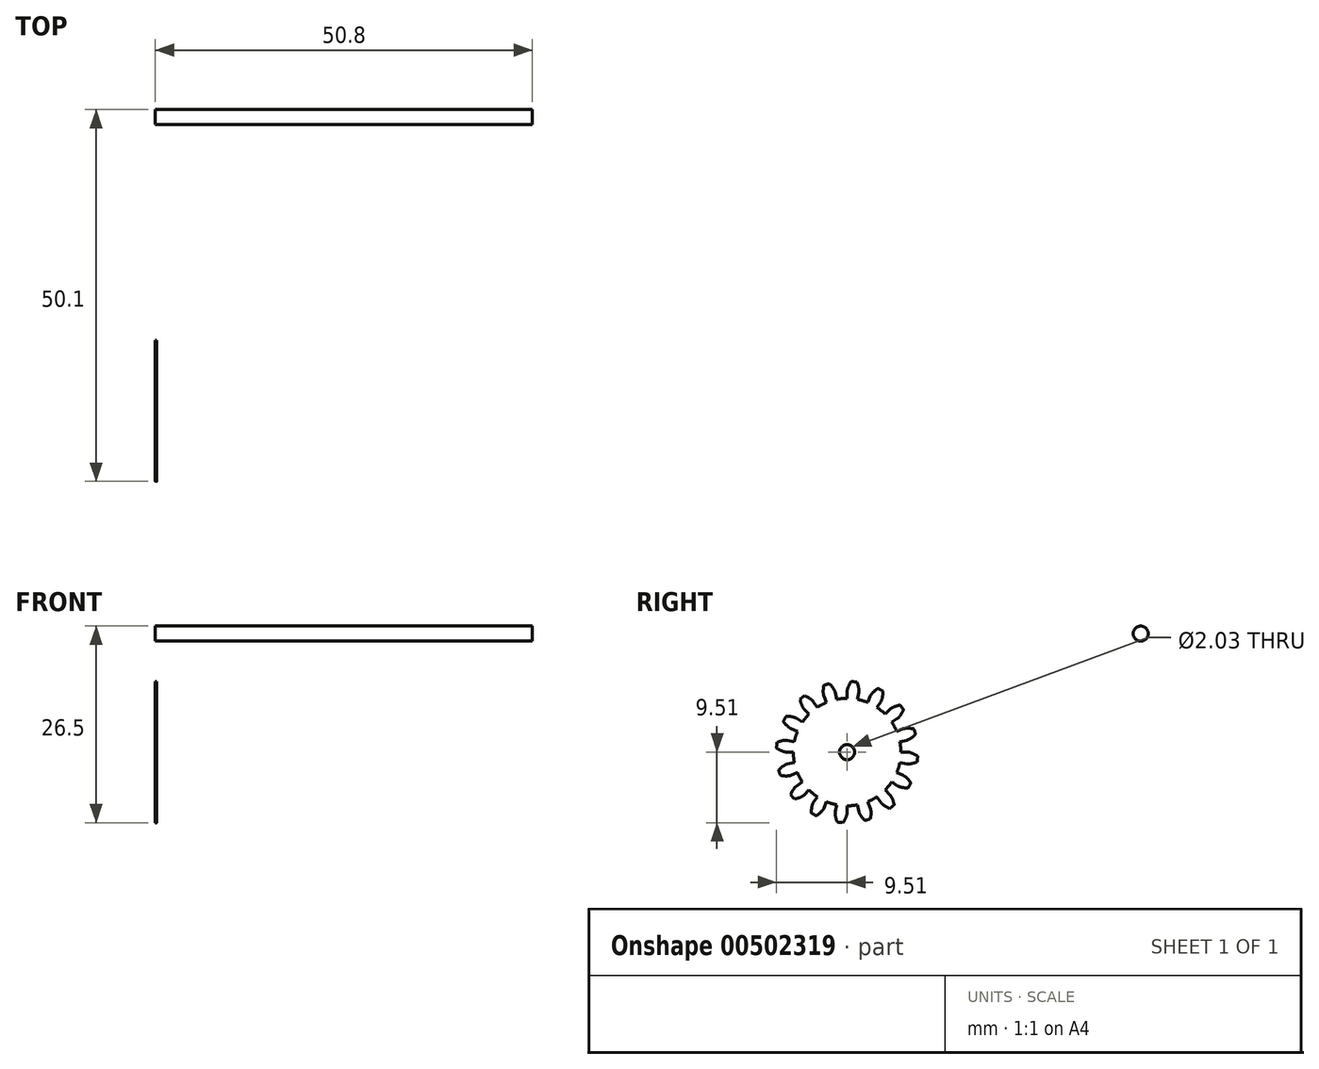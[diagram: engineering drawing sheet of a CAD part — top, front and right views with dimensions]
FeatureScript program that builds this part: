
annotation { "Feature Type Name" : "Feature", "Feature Type Description" : "" }
export const myFeature = defineFeature(function(context is Context, id is Id, definition is map)
    precondition{}
    {
        {
            assignVariable(context, id + "F0", {"name" : "NumberTeeth", "anyValue" : 16});
        }
        {
            assignVariable(context, id + "F1", {"name" : "GearThickness", "anyValue" : .16});
        }
        {
            var Q0;
            Q0=qCreatedBy(makeId("Right.planeOp"),FACE);
            var sketch = newSketch(context, id + "F2", { "sketchPlane" : qUnion([Q0])});
            skCircle(sketch, "E0", {"center": v(0, 0) * mm, "radius": 7.24 * mm});
            skCircle(sketch, "E1", {"center": v(0, 0) * mm, "radius": 8.2 * mm, "construction": true});
            skCircle(sketch, "E2", {"center": v(0, 0) * mm, "radius": 8.47 * mm, "construction": true});
            skCircle(sketch, "E3", {"center": v(0, 0) * mm, "radius": 9.53 * mm});
            skLineSegment(sketch, "E4", {"start": v(0, 0) * mm, "end": v(-8.2, 0) * mm, "construction": true});
            skLineSegment(sketch, "E5.1.0", {"start": v(0, 0) * mm, "end": v(-8.19, 0.4) * mm, "construction": true});
            skLineSegment(sketch, "E5.2.0", {"start": v(0, 0) * mm, "end": v(-8.16, 0.82) * mm, "construction": true});
            skLineSegment(sketch, "E5.3.0", {"start": v(0, 0) * mm, "end": v(-8.1, 1.22) * mm, "construction": true});
            skLineSegment(sketch, "E5.4.0", {"start": v(0, 0) * mm, "end": v(-8.03, 1.63) * mm, "construction": true});
            skLineSegment(sketch, "E5.5.0", {"start": v(0, 0) * mm, "end": v(-7.94, 2.03) * mm, "construction": true});
            skLineSegment(sketch, "E5.6.0", {"start": v(0, 0) * mm, "end": v(-7.83, 2.42) * mm, "construction": true});
            skLineSegment(sketch, "E5.7.0", {"start": v(0, 0) * mm, "end": v(-7.7, 2.81) * mm, "construction": true});
            skLineSegment(sketch, "E5.8.0", {"start": v(0, 0) * mm, "end": v(-7.55, 3.2) * mm, "construction": true});
            skLineSegment(sketch, "E5.9.0", {"start": v(0, 0) * mm, "end": v(-7.38, 3.57) * mm, "construction": true});
            skLineSegment(sketch, "E5.10.0", {"start": v(0, 0) * mm, "end": v(-7.2, 3.93) * mm, "construction": true});
            skLineSegment(sketch, "E5.11.0", {"start": v(0, 0) * mm, "end": v(-6.99, 4.28) * mm, "construction": true});
            skLineSegment(sketch, "E5.12.0", {"start": v(0, 0) * mm, "end": v(-6.77, 4.63) * mm, "construction": true});
            skLineSegment(sketch, "E5.13.0", {"start": v(0, 0) * mm, "end": v(-6.53, 4.96) * mm, "construction": true});
            skLineSegment(sketch, "E5.14.0", {"start": v(0, 0) * mm, "end": v(-6.27, 5.28) * mm, "construction": true});
            skLineSegment(sketch, "E5.anchor2", {"start": v(0, 0) * mm, "end": v(-6.27, 5.28) * mm, "construction": true});
            skLineSegment(sketch, "E6", {"start": v(-8.19, 0.4) * mm, "end": v(-8.2, 0) * mm, "construction": true});
            skLineSegment(sketch, "E7", {"start": v(-8.16, 0.82) * mm, "end": v(-8.24, 0) * mm, "construction": true});
            skLineSegment(sketch, "E8", {"start": v(-8.1, 1.22) * mm, "end": v(-8.29, 0) * mm, "construction": true});
            skLineSegment(sketch, "E9", {"start": v(-7.94, 2.03) * mm, "end": v(-8.45, 0.04) * mm, "construction": true});
            skLineSegment(sketch, "E10", {"start": v(-7.83, 2.42) * mm, "end": v(-8.56, 0.07) * mm, "construction": true});
            skLineSegment(sketch, "E11", {"start": v(-7.7, 2.81) * mm, "end": v(-8.68, 0.12) * mm, "construction": true});
            skLineSegment(sketch, "E12", {"start": v(-7.55, 3.2) * mm, "end": v(-8.83, 0.17) * mm, "construction": true});
            skLineSegment(sketch, "E13", {"start": v(-7.38, 3.57) * mm, "end": v(-8.99, 0.24) * mm, "construction": true});
            skLineSegment(sketch, "E14", {"start": v(-7.2, 3.93) * mm, "end": v(-9.16, 0.33) * mm, "construction": true});
            skLineSegment(sketch, "E15", {"start": v(-6.99, 4.28) * mm, "end": v(-9.34, 0.44) * mm, "construction": true});
            skLineSegment(sketch, "E16", {"start": v(-8.03, 1.63) * mm, "end": v(-8.36, 0.02) * mm, "construction": true});
            skLineSegment(sketch, "E17", {"start": v(-6.77, 4.63) * mm, "end": v(-9.54, 0.57) * mm, "construction": true});
            skLineSegment(sketch, "E18", {"start": v(-6.53, 4.96) * mm, "end": v(-9.75, 0.72) * mm, "construction": true});
            skLineSegment(sketch, "E19", {"start": v(-6.27, 5.28) * mm, "end": v(-9.97, 0.9) * mm, "construction": true});
            skLineSegment(sketch, "E20", {"start": v(0, 0) * mm, "end": v(-8.16, 0.8) * mm, "construction": true});
            skLineSegment(sketch, "E21", {"start": v(-7.24, 0) * mm, "end": v(-8.2, 0) * mm});
            skLineSegment(sketch, "E22.MirrorCS", {"start": v(-7.1, 1.41) * mm, "end": v(-8.04, 1.6) * mm});
            skFitSpline(sketch, "E23", {"points": [v(-8.2, 0) * mm, v(-8.2, 0) * mm, v(-8.24, 0) * mm, v(-8.29, 0) * mm, v(-8.36, 0.02) * mm, v(-8.45, 0.04) * mm, v(-8.56, 0.07) * mm, v(-8.68, 0.12) * mm, v(-8.83, 0.17) * mm, v(-8.99, 0.24) * mm, v(-9.16, 0.33) * mm, v(-9.34, 0.44) * mm, v(-9.54, 0.57) * mm, v(-9.75, 0.72) * mm, v(-9.97, 0.9) * mm], "startDerivative": vector(-0.86, 0) * mm, "endDerivative": vector(-1, 0.85) * mm});
            skLineSegment(sketch, "E24", {"start": v(-9.97, 0.9) * mm, "end": v(-15.8, 5.8) * mm, "construction": true});
            skFitSpline(sketch, "E25.MirrorCS", {"points": [v(-8.04, 1.6) * mm, v(-8.05, 1.6) * mm, v(-8.08, 1.6) * mm, v(-8.13, 1.6) * mm, v(-8.2, 1.6) * mm, v(-8.3, 1.6) * mm, v(-8.4, 1.6) * mm, v(-8.54, 1.58) * mm, v(-8.7, 1.55) * mm, v(-8.86, 1.51) * mm, v(-9.05, 1.46) * mm, v(-9.25, 1.4) * mm, v(-9.47, 1.3) * mm, v(-9.7, 1.2) * mm, v(-9.95, 1.07) * mm], "startDerivative": vector(-0.85, 0.17) * mm, "endDerivative": vector(-1.15, -0.63) * mm});
            skCircle(sketch, "E26", {"center": v(0, 0) * mm, "radius": 1.02 * mm});
            skCircle(sketch, "E27", {"center": v(39.57, 15.97) * mm, "radius": 1.02 * mm});
            skSolve(sketch);
        }
        {
            var Q0;
            {var subQ0=sQuery(id+"F2.wireOp",EDGE,"E0");var subQ27=makeQuery(id+"F2.imprint","INTERSECT",VERTEX,{"derivedFrom":[subQ0,sQuery(id+"F2.wireOp",EDGE,"10ea1024-8cf5-41f5-a75f-a634b86921f3.10.0")]});Q0=makeQuery(id+"F2.imprint","IMPRINT",FACE,{"disambiguationData":[TD([[makeQuery(id+"F2.imprint","IMPRINT",EDGE,{"disambiguationData":[TD([[subQ27,-1.0]])],"derivedFrom":subQ0}),1.0]])]});}
            var Q1;
            {var subQ0=sQuery(id+"F2.wireOp",EDGE,"10ea1024-8cf5-41f5-a75f-a634b86921f3.1.0");Q1=makeQuery(id+"F2.imprint","IMPRINT",FACE,{"disambiguationData":[TD([[makeQuery(id+"F2.imprint","IMPRINT",EDGE,{"derivedFrom":subQ0}),-1.0]])]});}
            var Q2;
            {var subQ7=sQuery(id+"F2.wireOp",EDGE,"10ea1024-8cf5-41f5-a75f-a634b86921f3.2.0");Q2=makeQuery(id+"F2.imprint","IMPRINT",FACE,{"disambiguationData":[TD([[makeQuery(id+"F2.imprint","IMPRINT",EDGE,{"derivedFrom":subQ7}),-1.0]])]});}
            var Q3;
            {var subQ8=sQuery(id+"F2.wireOp",EDGE,"10ea1024-8cf5-41f5-a75f-a634b86921f3.3.0");Q3=makeQuery(id+"F2.imprint","IMPRINT",FACE,{"disambiguationData":[TD([[makeQuery(id+"F2.imprint","IMPRINT",EDGE,{"derivedFrom":subQ8}),-1.0]])]});}
            var Q4;
            {var subQ2=sQuery(id+"F2.wireOp",EDGE,"10ea1024-8cf5-41f5-a75f-a634b86921f3.4.0");Q4=makeQuery(id+"F2.imprint","IMPRINT",FACE,{"disambiguationData":[TD([[makeQuery(id+"F2.imprint","IMPRINT",EDGE,{"derivedFrom":subQ2}),-1.0]])]});}
            var Q5;
            {var subQ8=sQuery(id+"F2.wireOp",EDGE,"10ea1024-8cf5-41f5-a75f-a634b86921f3.5.0");Q5=makeQuery(id+"F2.imprint","IMPRINT",FACE,{"disambiguationData":[TD([[makeQuery(id+"F2.imprint","IMPRINT",EDGE,{"derivedFrom":subQ8}),-1.0]])]});}
            var Q6;
            {var subQ3=sQuery(id+"F2.wireOp",EDGE,"10ea1024-8cf5-41f5-a75f-a634b86921f3.6.0");Q6=makeQuery(id+"F2.imprint","IMPRINT",FACE,{"disambiguationData":[TD([[makeQuery(id+"F2.imprint","IMPRINT",EDGE,{"derivedFrom":subQ3}),-1.0]])]});}
            var Q7;
            {var subQ0=sQuery(id+"F2.wireOp",EDGE,"10ea1024-8cf5-41f5-a75f-a634b86921f3.7.0");Q7=makeQuery(id+"F2.imprint","IMPRINT",FACE,{"disambiguationData":[TD([[makeQuery(id+"F2.imprint","IMPRINT",EDGE,{"derivedFrom":subQ0}),-1.0]])]});}
            var Q8;
            {var subQ5=sQuery(id+"F2.wireOp",EDGE,"10ea1024-8cf5-41f5-a75f-a634b86921f3.8.0");Q8=makeQuery(id+"F2.imprint","IMPRINT",FACE,{"disambiguationData":[TD([[makeQuery(id+"F2.imprint","IMPRINT",EDGE,{"derivedFrom":subQ5}),-1.0]])]});}
            var Q9;
            {var subQ1=sQuery(id+"F2.wireOp",EDGE,"10ea1024-8cf5-41f5-a75f-a634b86921f3.9.0");Q9=makeQuery(id+"F2.imprint","IMPRINT",FACE,{"disambiguationData":[TD([[makeQuery(id+"F2.imprint","IMPRINT",EDGE,{"derivedFrom":subQ1}),-1.0]])]});}
            var Q10;
            {var subQ5=sQuery(id+"F2.wireOp",EDGE,"10ea1024-8cf5-41f5-a75f-a634b86921f3.10.0");Q10=makeQuery(id+"F2.imprint","IMPRINT",FACE,{"disambiguationData":[TD([[makeQuery(id+"F2.imprint","IMPRINT",EDGE,{"derivedFrom":subQ5}),-1.0]])]});}
            var Q11;
            {var subQ8=sQuery(id+"F2.wireOp",EDGE,"10ea1024-8cf5-41f5-a75f-a634b86921f3.11.0");Q11=makeQuery(id+"F2.imprint","IMPRINT",FACE,{"disambiguationData":[TD([[makeQuery(id+"F2.imprint","IMPRINT",EDGE,{"derivedFrom":subQ8}),-1.0]])]});}
            var Q12;
            {var subQ2=sQuery(id+"F2.wireOp",EDGE,"10ea1024-8cf5-41f5-a75f-a634b86921f3.12.0");Q12=makeQuery(id+"F2.imprint","IMPRINT",FACE,{"disambiguationData":[TD([[makeQuery(id+"F2.imprint","IMPRINT",EDGE,{"derivedFrom":subQ2}),-1.0]])]});}
            var Q13;
            {var subQ3=sQuery(id+"F2.wireOp",EDGE,"10ea1024-8cf5-41f5-a75f-a634b86921f3.13.0");Q13=makeQuery(id+"F2.imprint","IMPRINT",FACE,{"disambiguationData":[TD([[makeQuery(id+"F2.imprint","IMPRINT",EDGE,{"derivedFrom":subQ3}),-1.0]])]});}
            var Q14;
            {var subQ0=sQuery(id+"F2.wireOp",EDGE,"10ea1024-8cf5-41f5-a75f-a634b86921f3.14.0");Q14=makeQuery(id+"F2.imprint","IMPRINT",FACE,{"disambiguationData":[TD([[makeQuery(id+"F2.imprint","IMPRINT",EDGE,{"derivedFrom":subQ0}),-1.0]])]});}
            var Q15;
            {var subQ6=sQuery(id+"F2.wireOp",EDGE,"10ea1024-8cf5-41f5-a75f-a634b86921f3.15.0");Q15=makeQuery(id+"F2.imprint","IMPRINT",FACE,{"disambiguationData":[TD([[makeQuery(id+"F2.imprint","IMPRINT",EDGE,{"derivedFrom":subQ6}),-1.0]])]});}
            var Q16;
            {var subQ5=sQuery(id+"F2.wireOp",EDGE,"10ea1024-8cf5-41f5-a75f-a634b86921f3.16.0");Q16=makeQuery(id+"F2.imprint","IMPRINT",FACE,{"disambiguationData":[TD([[makeQuery(id+"F2.imprint","IMPRINT",EDGE,{"derivedFrom":subQ5}),-1.0]])]});}
            var Q17;
            {var subQ7=sQuery(id+"F2.wireOp",EDGE,"10ea1024-8cf5-41f5-a75f-a634b86921f3.17.0");Q17=makeQuery(id+"F2.imprint","IMPRINT",FACE,{"disambiguationData":[TD([[makeQuery(id+"F2.imprint","IMPRINT",EDGE,{"derivedFrom":subQ7}),-1.0]])]});}
            var Q18;
            {var subQ5=sQuery(id+"F2.wireOp",EDGE,"10ea1024-8cf5-41f5-a75f-a634b86921f3.18.0");Q18=makeQuery(id+"F2.imprint","IMPRINT",FACE,{"disambiguationData":[TD([[makeQuery(id+"F2.imprint","IMPRINT",EDGE,{"derivedFrom":subQ5}),-1.0]])]});}
            var Q19;
            {var subQ8=sQuery(id+"F2.wireOp",EDGE,"10ea1024-8cf5-41f5-a75f-a634b86921f3.19.0");Q19=makeQuery(id+"F2.imprint","IMPRINT",FACE,{"disambiguationData":[TD([[makeQuery(id+"F2.imprint","IMPRINT",EDGE,{"derivedFrom":subQ8}),-1.0]])]});}
            var Q20;
            {var subQ8=sQuery(id+"F2.wireOp",EDGE,"E21");Q20=makeQuery(id+"F2.imprint","IMPRINT",FACE,{"disambiguationData":[TD([[makeQuery(id+"F2.imprint","IMPRINT",EDGE,{"derivedFrom":subQ8}),-1.0]])]});}
            extrude(context, id + "F3", {"entities" : qUnion([Q0, Q1, Q2, Q3, Q4, Q5, Q6, Q7, Q8, Q9, Q10, Q11, Q12, Q13, Q14, Q15, Q16, Q17, Q18, Q19, Q20]), "depth" : (getVariable(context, 'GearThickness')) * mm});
        }
        {
            var Q0;
            Q0=makeQuery(id+"F3.opExtrude","SWEPT_FACE",FACE,{"disambiguationData":[OSD([sQuery(id+"F2.wireOp",EDGE,"E25.MirrorCS")])]});
            var Q1;
            Q1=makeQuery(id+"F3.opExtrude","SWEPT_FACE",FACE,{"disambiguationData":[OSD([sQuery(id+"F2.wireOp",EDGE,"E23")])]});
            var Q2;
            Q2=makeQuery(id+"F3.opExtrude","SWEPT_FACE",FACE,{"disambiguationData":[OSD([sQuery(id+"F2.wireOp",EDGE,"E3")])]});
            var Q3;
            Q3=makeQuery(id+"F3.opExtrude","SWEPT_FACE",FACE,{"disambiguationData":[OSD([sQuery(id+"F2.wireOp",EDGE,"E22.MirrorCS")])]});
            var Q4;
            Q4=makeQuery(id+"F3.opExtrude","SWEPT_FACE",FACE,{"disambiguationData":[OSD([sQuery(id+"F2.wireOp",EDGE,"E21")])]});
            var Q5;
            Q5=makeQuery(id+"F3.opExtrude","SWEPT_FACE",FACE,{"disambiguationData":[OSD([sQuery(id+"F2.wireOp",EDGE,"E0")])]});
            circularPattern(context, id + "F4", {"faces" : qUnion([Q0, Q1, Q2, Q3, Q4]), "axis" : qUnion([Q5]), "angle" : 360 * degree, "instanceCount" : getVariable(context, 'NumberTeeth'), "equalSpace" : true, "patternType" : PatternType.FACE});
        }
        {
            var Q0;
            Q0=makeQuery(id+"F2.imprint","IMPRINT",FACE,{"disambiguationData":[TD([[makeQuery(id+"F2.imprint","IMPRINT",EDGE,{"derivedFrom":sQuery(id+"F2.wireOp",EDGE,"E27")}),1.0]])]});
            extrude(context, id + "F5", {"entities" : qUnion([Q0]), "depth" : 50.8 * mm});
        }
    });
